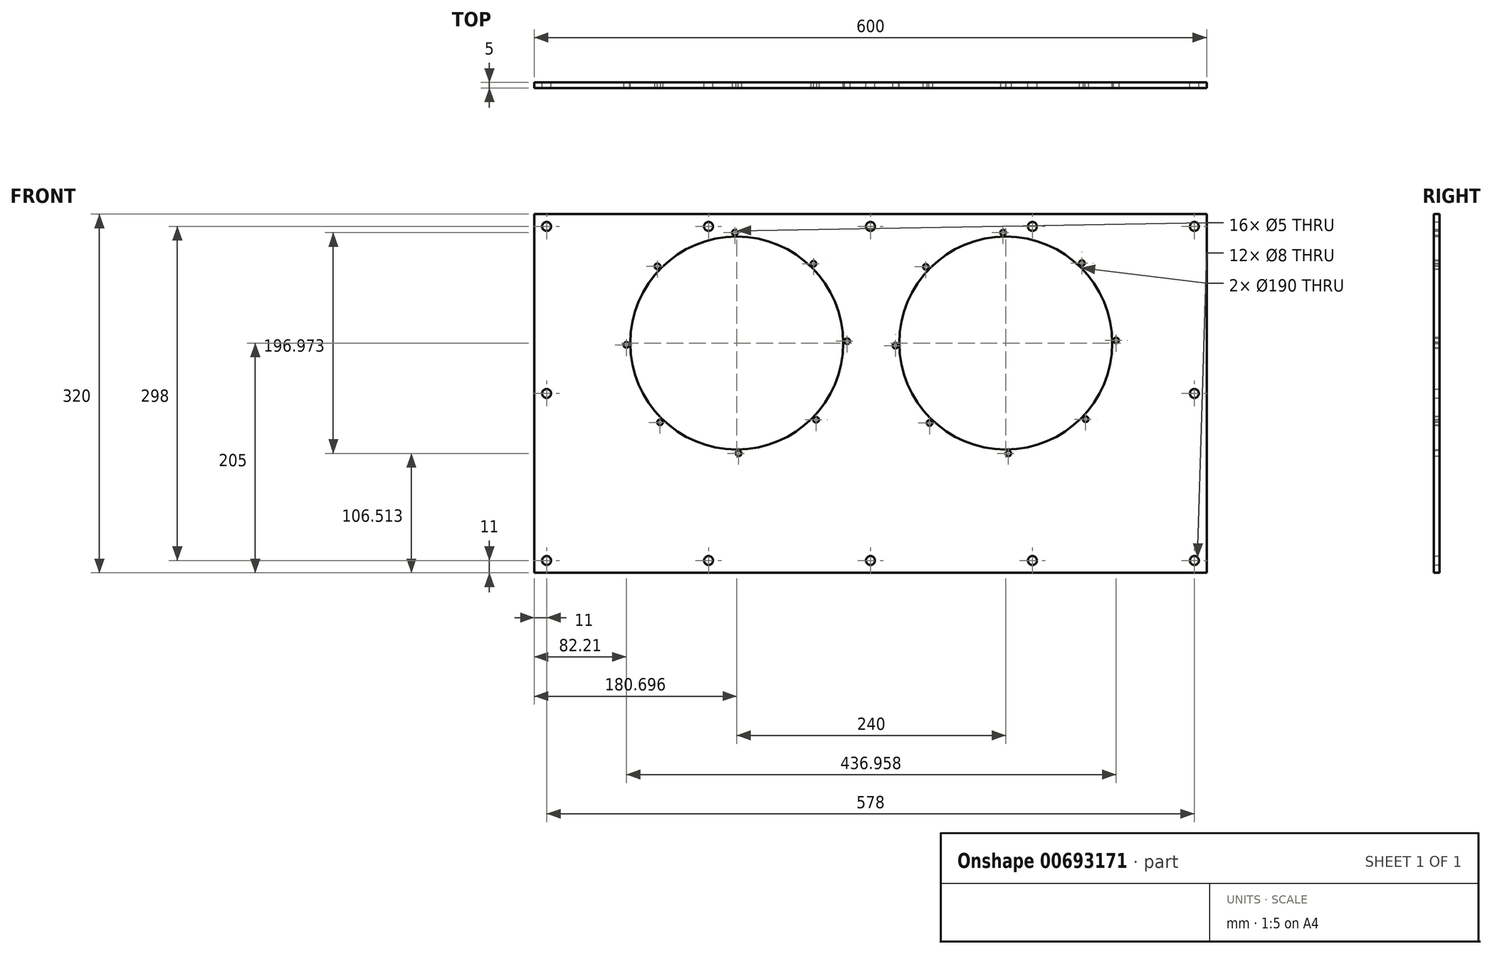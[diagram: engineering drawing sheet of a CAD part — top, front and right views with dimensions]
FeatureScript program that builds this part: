
annotation { "Feature Type Name" : "Feature", "Feature Type Description" : "" }
export const myFeature = defineFeature(function(context is Context, id is Id, definition is map)
    precondition{}
    {
        {
            var Q0;
            Q0=qCreatedBy(makeId("Front.planeOp"),FACE);
            var sketch = newSketch(context, id + "F0", { "sketchPlane" : qUnion([Q0])});
            skLineSegment(sketch, "E0.bottom", {"start": v(-300, 160) * mm, "end": v(300, 160) * mm});
            skLineSegment(sketch, "E0.top", {"start": v(-300, -160) * mm, "end": v(300, -160) * mm});
            skLineSegment(sketch, "E0.left", {"start": v(-300, 160) * mm, "end": v(-300, -160) * mm});
            skLineSegment(sketch, "E0.right", {"start": v(300, 160) * mm, "end": v(300, -160) * mm});
            skPoint(sketch, "E0.middle", {"position": v(0, 0) * mm});
            skLineSegment(sketch, "E1.bottom", {"start": v(-291.1, 150) * mm, "end": v(292.55, 150) * mm, "construction": true});
            skLineSegment(sketch, "E1.top", {"start": v(-291.1, -60) * mm, "end": v(292.55, -60) * mm, "construction": true});
            skLineSegment(sketch, "E1.left", {"start": v(-291.1, 150) * mm, "end": v(-291.1, -60) * mm, "construction": true});
            skLineSegment(sketch, "E1.right", {"start": v(292.55, 150) * mm, "end": v(292.55, -60) * mm, "construction": true});
            skLineSegment(sketch, "E2", {"start": v(-291.1, 45) * mm, "end": v(292.55, 45) * mm, "construction": true});
            skCircle(sketch, "E3", {"center": v(-119.3, 45) * mm, "radius": 95 * mm});
            skCircle(sketch, "E4", {"center": v(120.7, 45) * mm, "radius": 95 * mm});
            skSolve(sketch);
        }
        {
            var Q0;
            Q0 = qSketchRegion(id + "F0", true);
            extrude(context, id + "F1", {"entities" : qUnion([Q0]), "depth" : 5 * mm, "offsetDistance" : 25 * mm});
        }
        {
            var Q0;
            Q0=makeQuery(id+"F1.opExtrude","CAP_FACE",FACE,{"disambiguationData":[OSD([sQuery(id+"F0.wireOp",EDGE,"E0.bottom"),sQuery(id+"F0.wireOp",EDGE,"E0.top"),sQuery(id+"F0.wireOp",EDGE,"E0.left"),sQuery(id+"F0.wireOp",EDGE,"E0.right"),sQuery(id+"F0.wireOp",EDGE,"E3"),sQuery(id+"F0.wireOp",EDGE,"E4")])],"isStart":false});
            var sketch = newSketch(context, id + "F2", { "sketchPlane" : qUnion([Q0])});
            skCircle(sketch, "E5", {"center": v(-119.3, 45) * mm, "radius": 98.5 * mm, "construction": true});
            skCircle(sketch, "E6", {"center": v(120.7, 45) * mm, "radius": 98.5 * mm, "construction": true});
            skCircle(sketch, "E7", {"center": v(-120.93, 143.49) * mm, "radius": 2.5 * mm});
            skCircle(sketch, "E8", {"center": v(118.34, 143.47) * mm, "radius": 2.5 * mm});
            skCircle(sketch, "E9.1.0", {"center": v(-190.1, 113.49) * mm, "radius": 2.5 * mm});
            skCircle(sketch, "E9.2.0", {"center": v(-217.8, 43.37) * mm, "radius": 2.5 * mm});
            skCircle(sketch, "E9.3.0", {"center": v(-187.8, -25.8) * mm, "radius": 2.5 * mm});
            skCircle(sketch, "E9.4.0", {"center": v(-117.68, -53.49) * mm, "radius": 2.5 * mm});
            skCircle(sketch, "E9.5.0", {"center": v(-48.51, -23.49) * mm, "radius": 2.5 * mm});
            skCircle(sketch, "E9.6.0", {"center": v(-20.82, 46.63) * mm, "radius": 2.5 * mm});
            skCircle(sketch, "E9.7.0", {"center": v(-50.81, 115.8) * mm, "radius": 2.5 * mm});
            skCircle(sketch, "E10.1.0", {"center": v(49.4, 112.96) * mm, "radius": 2.5 * mm});
            skCircle(sketch, "E10.2.0", {"center": v(22.22, 42.64) * mm, "radius": 2.5 * mm});
            skCircle(sketch, "E10.3.0", {"center": v(52.73, -26.3) * mm, "radius": 2.5 * mm});
            skCircle(sketch, "E10.4.0", {"center": v(123.05, -53.47) * mm, "radius": 2.5 * mm});
            skCircle(sketch, "E10.5.0", {"center": v(192, -22.96) * mm, "radius": 2.5 * mm});
            skCircle(sketch, "E10.6.0", {"center": v(219.17, 47.36) * mm, "radius": 2.5 * mm});
            skCircle(sketch, "E10.7.0", {"center": v(188.66, 116.3) * mm, "radius": 2.5 * mm});
            skSolve(sketch);
        }
        {
            var Q0;
            Q0 = qSketchRegion(id + "F2", true);
            extrude(context, id + "F3", {"entities" : qUnion([Q0]), "operationType" : NewBodyOperationType.REMOVE, "oppositeDirection" : true, "depth" : 25 * mm, "offsetDistance" : 25 * mm});
        }
        {
            var Q0;
            Q0=makeQuery(id+"F1.opExtrude","CAP_FACE",FACE,{"disambiguationData":[OSD([sQuery(id+"F0.wireOp",EDGE,"E0.bottom"),sQuery(id+"F0.wireOp",EDGE,"E0.top"),sQuery(id+"F0.wireOp",EDGE,"E0.left"),sQuery(id+"F0.wireOp",EDGE,"E0.right"),sQuery(id+"F0.wireOp",EDGE,"E3"),sQuery(id+"F0.wireOp",EDGE,"E4")])],"isStart":true});
            var sketch = newSketch(context, id + "F4", { "sketchPlane" : qUnion([Q0])});
            skLineSegment(sketch, "E11.0", {"start": v(289, 149) * mm, "end": v(-289, 149) * mm, "construction": true});
            skLineSegment(sketch, "E11.1", {"start": v(289, -149) * mm, "end": v(289, 149) * mm, "construction": true});
            skLineSegment(sketch, "E11.2", {"start": v(-289, -149) * mm, "end": v(289, -149) * mm, "construction": true});
            skLineSegment(sketch, "E11.3", {"start": v(-289, 149) * mm, "end": v(-289, -149) * mm, "construction": true});
            skCircle(sketch, "E12", {"center": v(289, 149) * mm, "radius": 4 * mm});
            skCircle(sketch, "E13.0.1.0", {"center": v(289, -149) * mm, "radius": 4 * mm});
            skCircle(sketch, "E13.1.0.0", {"center": v(144.5, 149) * mm, "radius": 4 * mm});
            skCircle(sketch, "E13.1.1.0", {"center": v(144.5, -149) * mm, "radius": 4 * mm});
            skCircle(sketch, "E13.2.0.0", {"center": v(0, 149) * mm, "radius": 4 * mm});
            skCircle(sketch, "E13.2.1.0", {"center": v(0, -149) * mm, "radius": 4 * mm});
            skCircle(sketch, "E13.3.0.0", {"center": v(-144.5, 149) * mm, "radius": 4 * mm});
            skCircle(sketch, "E13.3.1.0", {"center": v(-144.5, -149) * mm, "radius": 4 * mm});
            skCircle(sketch, "E13.4.0.0", {"center": v(-289, 149) * mm, "radius": 4 * mm});
            skCircle(sketch, "E13.4.1.0", {"center": v(-289, -149) * mm, "radius": 4 * mm});
            skLineSegment(sketch, "E13.direction1", {"start": v(289, 149) * mm, "end": v(144.5, 149) * mm, "construction": true});
            skLineSegment(sketch, "E13.direction2", {"start": v(289, 149) * mm, "end": v(289, -149) * mm, "construction": true});
            skCircle(sketch, "E14", {"center": v(-289, 0) * mm, "radius": 4 * mm});
            skCircle(sketch, "E15", {"center": v(289, 0) * mm, "radius": 4 * mm});
            skSolve(sketch);
        }
        {
            var Q0;
            Q0 = qSketchRegion(id + "F4", true);
            extrude(context, id + "F5", {"entities" : qUnion([Q0]), "operationType" : NewBodyOperationType.REMOVE, "oppositeDirection" : true, "depth" : 25 * mm, "offsetDistance" : 25 * mm});
        }
    });
